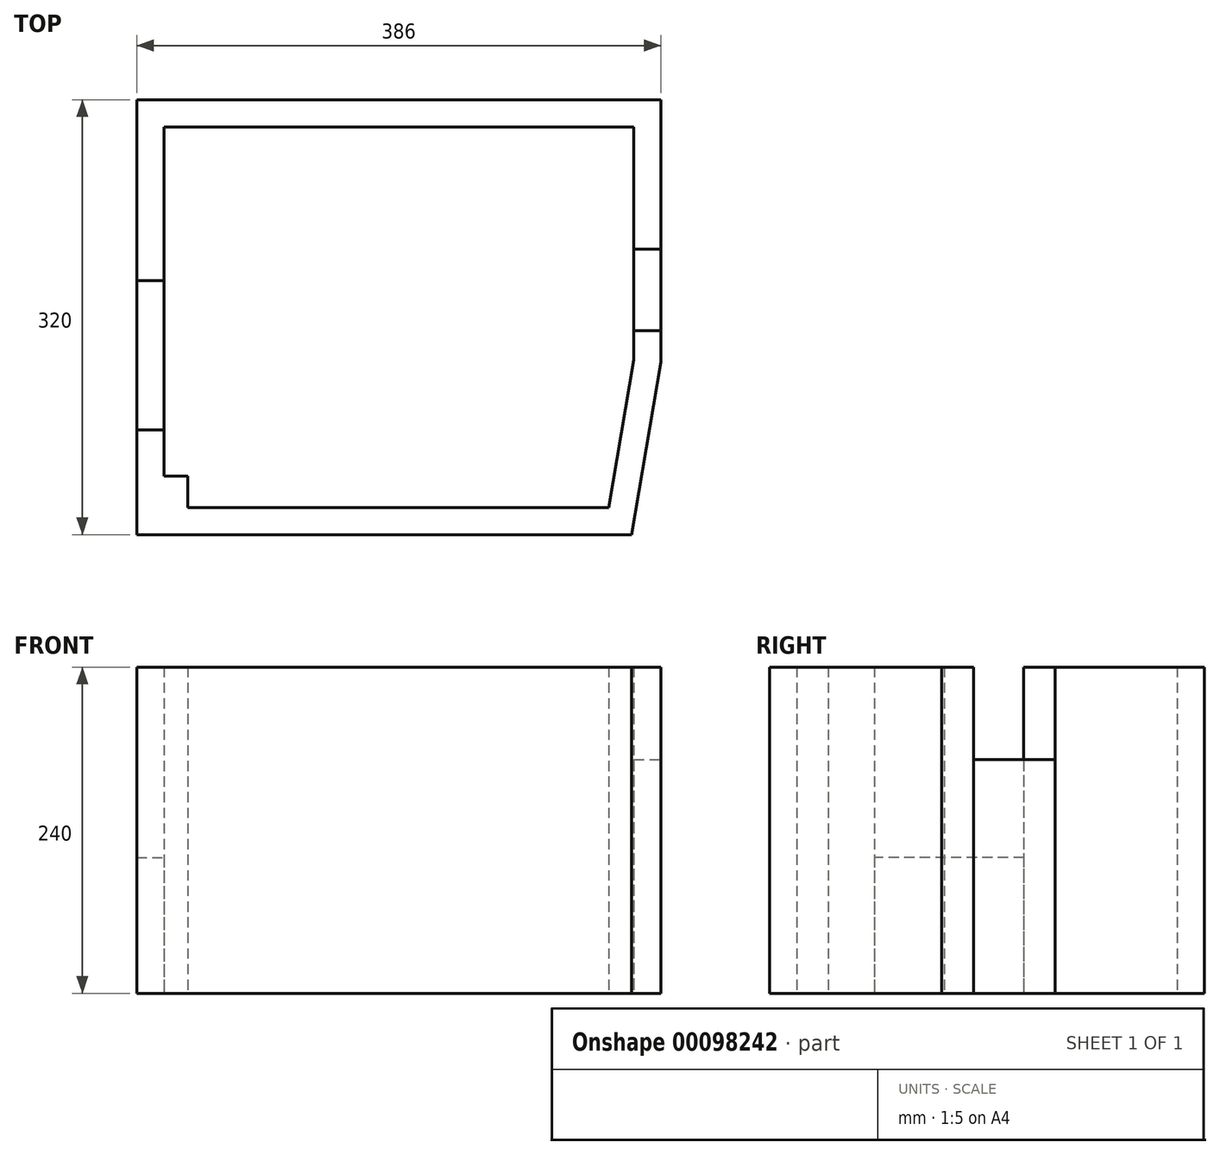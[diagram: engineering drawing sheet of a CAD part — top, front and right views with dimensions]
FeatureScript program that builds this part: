
annotation { "Feature Type Name" : "Feature", "Feature Type Description" : "" }
export const myFeature = defineFeature(function(context is Context, id is Id, definition is map)
    precondition{}
    {
        {
            var Q0;
            Q0=qCreatedBy(makeId("Top.planeOp"),FACE);
            var sketch = newSketch(context, id + "F0", { "sketchPlane" : qUnion([Q0])});
            skLineSegment(sketch, "E0.bottom", {"start": v(-164.5, 150) * mm, "end": v(181.5, 150) * mm});
            skLineSegment(sketch, "E0.left", {"start": v(-164.5, 150) * mm, "end": v(-164.5, -130) * mm});
            skLineSegment(sketch, "E0.right", {"start": v(181.5, 150) * mm, "end": v(181.5, -21.57) * mm});
            skLineSegment(sketch, "E1", {"start": v(-164.5, -130) * mm, "end": v(163, -130) * mm});
            skLineSegment(sketch, "E2", {"start": v(163, -130) * mm, "end": v(181.5, -21.57) * mm});
            skLineSegment(sketch, "E3.0", {"start": v(201.5, 170) * mm, "end": v(201.5, -23.26) * mm});
            skLineSegment(sketch, "E3.1", {"start": v(-184.5, 170) * mm, "end": v(201.5, 170) * mm});
            skLineSegment(sketch, "E3.2", {"start": v(179.87, -150) * mm, "end": v(201.5, -23.26) * mm});
            skLineSegment(sketch, "E3.3", {"start": v(-184.5, -150) * mm, "end": v(179.87, -150) * mm});
            skLineSegment(sketch, "E3.4", {"start": v(-184.5, 170) * mm, "end": v(-184.5, -150) * mm});
            skLineSegment(sketch, "E4.bottom", {"start": v(-164.5, -107) * mm, "end": v(-147, -107) * mm});
            skLineSegment(sketch, "E4.top", {"start": v(-164.5, -130) * mm, "end": v(-147, -130) * mm});
            skLineSegment(sketch, "E4.left", {"start": v(-164.5, -107) * mm, "end": v(-164.5, -130) * mm});
            skLineSegment(sketch, "E4.right", {"start": v(-147, -107) * mm, "end": v(-147, -130) * mm});
            skLineSegment(sketch, "E5.bottom", {"start": v(-184.5, 37) * mm, "end": v(-164.5, 37) * mm});
            skLineSegment(sketch, "E5.top", {"start": v(-184.5, -73) * mm, "end": v(-164.5, -73) * mm});
            skLineSegment(sketch, "E5.left", {"start": v(-184.5, 37) * mm, "end": v(-184.5, -73) * mm});
            skLineSegment(sketch, "E5.right", {"start": v(-164.5, 37) * mm, "end": v(-164.5, -73) * mm});
            skLineSegment(sketch, "E6.bottom", {"start": v(181.5, 60) * mm, "end": v(201.5, 60) * mm});
            skLineSegment(sketch, "E6.top", {"start": v(181.5, 0) * mm, "end": v(201.5, 0) * mm});
            skLineSegment(sketch, "E6.left", {"start": v(181.5, 60) * mm, "end": v(181.5, 0) * mm});
            skLineSegment(sketch, "E6.right", {"start": v(201.5, 60) * mm, "end": v(201.5, 0) * mm});
            skSolve(sketch);
        }
        {
            var Q0;
            Q0=makeQuery(id+"F0.imprint","IMPRINT",FACE,{"disambiguationData":[TD([[makeQuery(id+"F0.imprint","IMPRINT",EDGE,{"derivedFrom":sQuery(id+"F0.wireOp",EDGE,"E4.bottom")}),-1.0]])]});
            var Q1;
            Q1=makeQuery(id+"F0.imprint","IMPRINT",FACE,{"disambiguationData":[TD([[makeQuery(id+"F0.imprint","IMPRINT",EDGE,{"derivedFrom":sQuery(id+"F0.wireOp",EDGE,"E1")}),-1.0]])]});
            var Q2;
            {var subQ5=sQuery(id+"F0.wireOp",EDGE,"E0.bottom");Q2=makeQuery(id+"F0.imprint","IMPRINT",FACE,{"disambiguationData":[TD([[makeQuery(id+"F0.imprint","IMPRINT",EDGE,{"derivedFrom":subQ5}),1.0]])]});}
            extrude(context, id + "F1", {"entities" : qUnion([Q0, Q1, Q2]), "depth" : 240 * mm});
        }
        {
            var Q0;
            Q0=makeQuery(id+"F0.imprint","IMPRINT",FACE,{"disambiguationData":[TD([[makeQuery(id+"F0.imprint","IMPRINT",EDGE,{"derivedFrom":sQuery(id+"F0.wireOp",EDGE,"E6.bottom")}),-1.0]])]});
            extrude(context, id + "F2", {"entities" : qUnion([Q0]), "depth" : 172 * mm});
        }
        {
            var Q0;
            Q0=makeQuery(id+"F0.imprint","IMPRINT",FACE,{"disambiguationData":[TD([[makeQuery(id+"F0.imprint","IMPRINT",EDGE,{"derivedFrom":sQuery(id+"F0.wireOp",EDGE,"E5.bottom")}),-1.0]])]});
            extrude(context, id + "F3", {"entities" : qUnion([Q0]), "depth" : 100 * mm});
        }
    });
